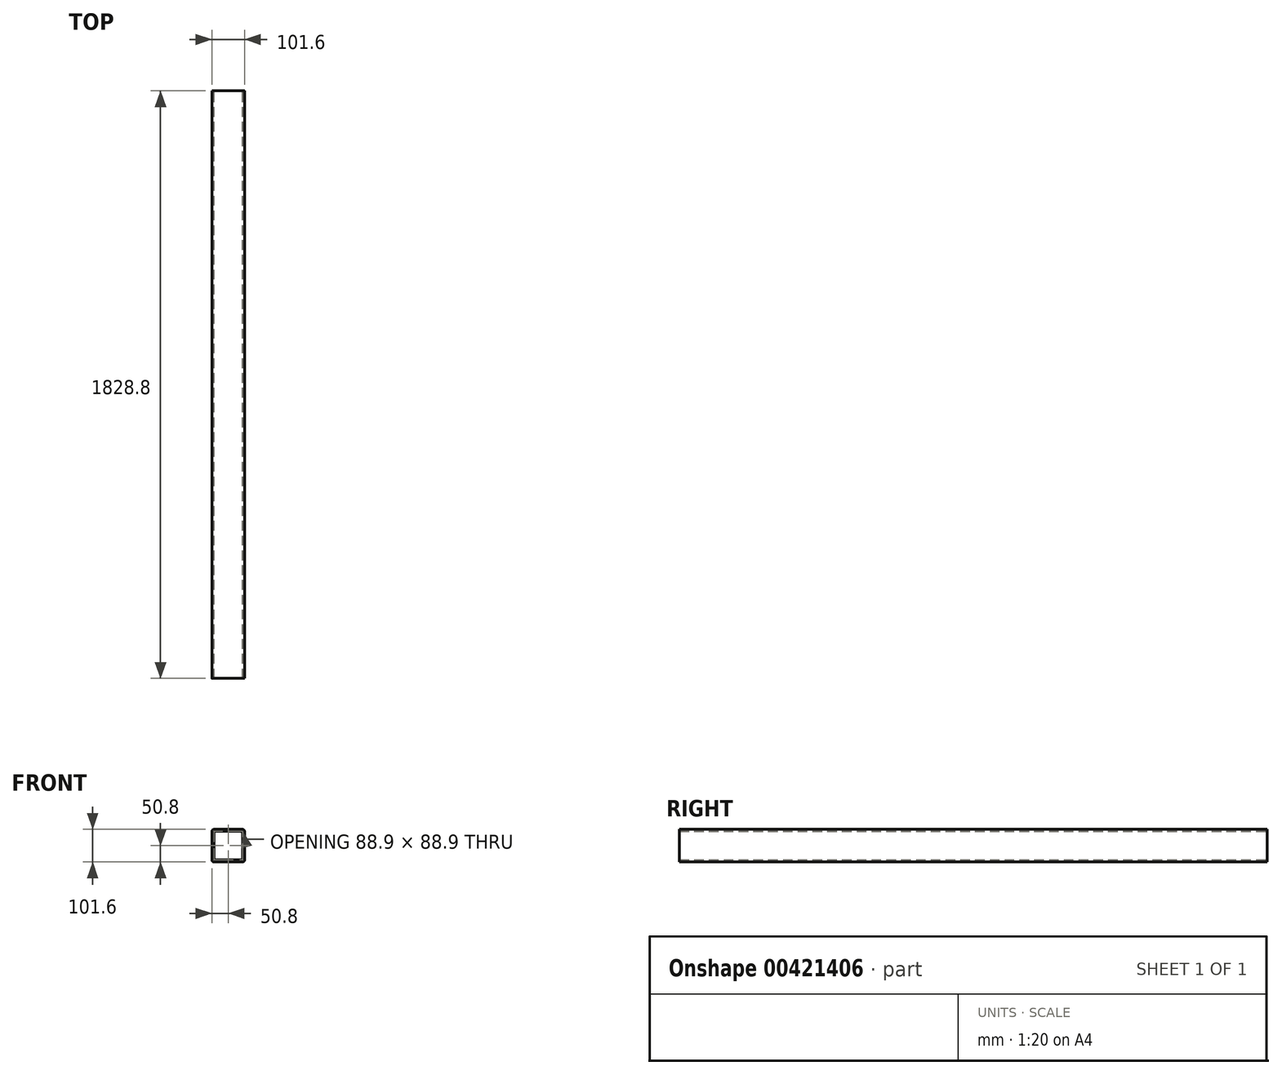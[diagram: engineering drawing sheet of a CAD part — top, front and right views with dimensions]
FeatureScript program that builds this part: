
annotation { "Feature Type Name" : "Feature", "Feature Type Description" : "" }
export const myFeature = defineFeature(function(context is Context, id is Id, definition is map)
    precondition{}
    {
        {
            var Q0;
            Q0=qCreatedBy(makeId("Front.planeOp"),FACE);
            var sketch = newSketch(context, id + "F0", { "sketchPlane" : qUnion([Q0])});
            skLineSegment(sketch, "E0.bottom", {"start": v(44.45, -44.45) * mm, "end": v(-44.45, -44.45) * mm});
            skLineSegment(sketch, "E0.top", {"start": v(44.45, 44.45) * mm, "end": v(-44.45, 44.45) * mm});
            skLineSegment(sketch, "E0.left", {"start": v(44.45, -44.45) * mm, "end": v(44.45, 44.45) * mm});
            skLineSegment(sketch, "E0.right", {"start": v(-44.45, -44.45) * mm, "end": v(-44.45, 44.45) * mm});
            skPoint(sketch, "E0.middle", {"position": v(0, 0) * mm});
            skLineSegment(sketch, "E1.bottom", {"start": v(50.8, -50.8) * mm, "end": v(-50.8, -50.8) * mm});
            skLineSegment(sketch, "E1.top", {"start": v(50.8, 50.8) * mm, "end": v(-50.8, 50.8) * mm});
            skLineSegment(sketch, "E1.left", {"start": v(50.8, -50.8) * mm, "end": v(50.8, 50.8) * mm});
            skLineSegment(sketch, "E1.right", {"start": v(-50.8, -50.8) * mm, "end": v(-50.8, 50.8) * mm});
            skSolve(sketch);
        }
        {
            var Q0;
            Q0 = qSketchRegion(id + "F0", true);
            extrude(context, id + "F1", {"entities" : qUnion([Q0]), "endBound" : BoundingType.SYMMETRIC, "depth" : 1828.8 * mm});
        }
        {
            var Q0;
            Q0=makeQuery(id+"F1.opExtrude","SWEPT_EDGE",EDGE,{"disambiguationData":[OSD([sQuery(id+"F0.wireOp",EDGE,"E1.top"),sQuery(id+"F0.wireOp",EDGE,"E1.right")])]});
            var Q1;
            Q1=makeQuery(id+"F1.opExtrude","SWEPT_EDGE",EDGE,{"disambiguationData":[OSD([sQuery(id+"F0.wireOp",EDGE,"E1.top"),sQuery(id+"F0.wireOp",EDGE,"E1.left")])]});
            var Q2;
            Q2=makeQuery(id+"F1.opExtrude","SWEPT_EDGE",EDGE,{"disambiguationData":[OSD([sQuery(id+"F0.wireOp",EDGE,"E0.bottom"),sQuery(id+"F0.wireOp",EDGE,"E0.left")])]});
            var Q3;
            Q3=makeQuery(id+"F1.opExtrude","SWEPT_EDGE",EDGE,{"disambiguationData":[OSD([sQuery(id+"F0.wireOp",EDGE,"E0.bottom"),sQuery(id+"F0.wireOp",EDGE,"E0.right")])]});
            var Q4;
            Q4=makeQuery(id+"F1.opExtrude","SWEPT_EDGE",EDGE,{"disambiguationData":[OSD([sQuery(id+"F0.wireOp",EDGE,"E0.top"),sQuery(id+"F0.wireOp",EDGE,"E0.left")])]});
            var Q5;
            Q5=makeQuery(id+"F1.opExtrude","SWEPT_EDGE",EDGE,{"disambiguationData":[OSD([sQuery(id+"F0.wireOp",EDGE,"E0.top"),sQuery(id+"F0.wireOp",EDGE,"E0.right")])]});
            var Q6;
            Q6=makeQuery(id+"F1.opExtrude","SWEPT_EDGE",EDGE,{"disambiguationData":[OSD([sQuery(id+"F0.wireOp",EDGE,"E1.bottom"),sQuery(id+"F0.wireOp",EDGE,"E1.left")])]});
            var Q7;
            Q7=makeQuery(id+"F1.opExtrude","SWEPT_EDGE",EDGE,{"disambiguationData":[OSD([sQuery(id+"F0.wireOp",EDGE,"E1.bottom"),sQuery(id+"F0.wireOp",EDGE,"E1.right")])]});
            fillet(context, id + "F2", {"entities" : qUnion([Q0, Q1, Q2, Q3, Q4, Q5, Q6, Q7]), "radius" : 6.35 * mm, "tangentPropagation" : true, "allowEdgeOverflow" : false});
        }
    });
